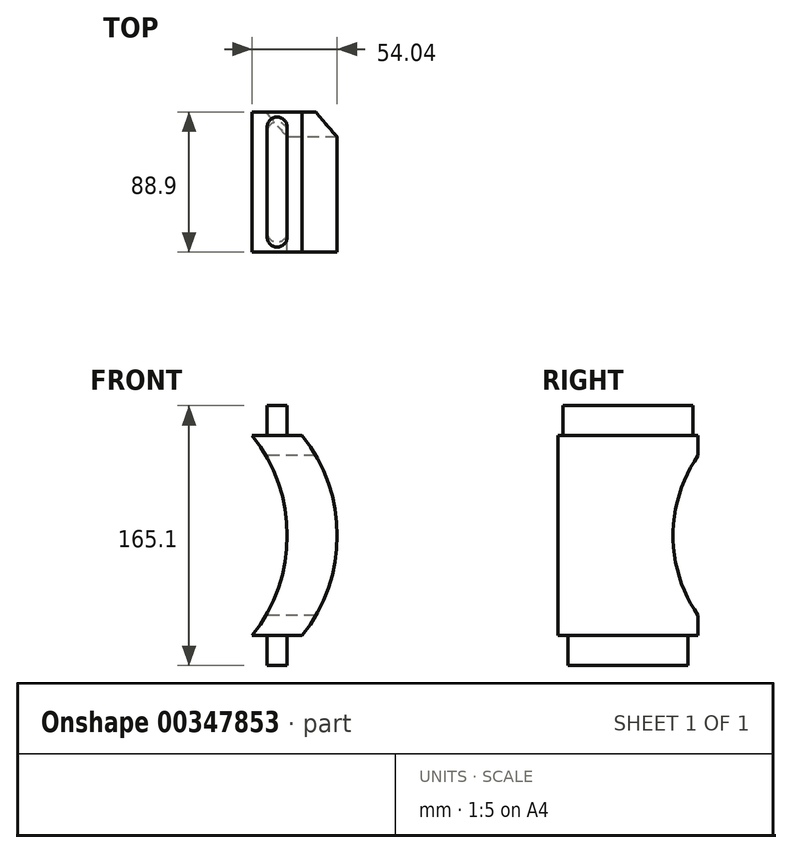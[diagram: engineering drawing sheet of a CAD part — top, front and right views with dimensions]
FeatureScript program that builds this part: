
annotation { "Feature Type Name" : "Feature", "Feature Type Description" : "" }
export const myFeature = defineFeature(function(context is Context, id is Id, definition is map)
    precondition{}
    {
        {
            var Q0;
            Q0=qCreatedBy(makeId("Front.planeOp"),FACE);
            var sketch = newSketch(context, id + "F0", { "sketchPlane" : qUnion([Q0])});
            skLineSegment(sketch, "E0.bottom", {"start": v(-32.55, 106.2) * mm, "end": v(-64.3, 106.2) * mm});
            skLineSegment(sketch, "E0.top", {"start": v(-32.55, -20.8) * mm, "end": v(-64.3, -20.8) * mm});
            skLineSegment(sketch, "E0.left", {"start": v(-32.55, 106.2) * mm, "end": v(-32.55, -20.8) * mm});
            skArc(sketch, "E1", {"start": v(-64.3, -20.8) * mm, "mid": v(-42, 42.7) * mm, "end": v(-64.3, 106.2) * mm});
            skArc(sketch, "E2", {"start": v(-32.55, -20.8) * mm, "mid": v(-10.26, 42.7) * mm, "end": v(-32.55, 106.2) * mm});
            skSolve(sketch);
        }
        {
            var Q0;
            Q0 = qSketchRegion(id + "F0", true);
            extrude(context, id + "F1", {"entities" : qUnion([Q0]), "depth" : 88.9 * mm});
        }
        {
            var Q0;
            Q0=makeQuery(id+"F1.opExtrude","SWEPT_FACE",FACE,{"disambiguationData":[OSD([sQuery(id+"F0.wireOp",EDGE,"E0.top")])]});
            var sketch = newSketch(context, id + "F2", { "sketchPlane" : qUnion([Q0])});
            skLineSegment(sketch, "E3", {"start": v(-48.42, 88.9) * mm, "end": v(-48.42, 0) * mm, "construction": true});
            skLineSegment(sketch, "E4", {"start": v(-32.55, 44.45) * mm, "end": v(-64.3, 44.45) * mm, "construction": true});
            skArc(sketch, "E5", {"start": v(-42.07, 76.2) * mm, "mid": v(-48.42, 82.55) * mm, "end": v(-54.77, 76.2) * mm});
            skArc(sketch, "E6", {"start": v(-54.77, 12.7) * mm, "mid": v(-48.42, 6.35) * mm, "end": v(-42.07, 12.7) * mm});
            skLineSegment(sketch, "E7", {"start": v(-54.77, 76.2) * mm, "end": v(-54.77, 12.7) * mm});
            skLineSegment(sketch, "E8", {"start": v(-42.07, 76.2) * mm, "end": v(-42.07, 12.7) * mm});
            skLineSegment(sketch, "E9", {"start": v(-54.77, 44.45) * mm, "end": v(-42.07, 44.45) * mm, "construction": true});
            skSolve(sketch);
        }
        {
            var Q0;
            Q0 = qSketchRegion(id + "F2", true);
            extrude(context, id + "F3", {"entities" : qUnion([Q0]), "operationType" : NewBodyOperationType.ADD, "depth" : 19.05 * mm});
        }
        {
            var Q0;
            Q0=makeQuery(id+"F1.opExtrude","SWEPT_FACE",FACE,{"disambiguationData":[OSD([sQuery(id+"F0.wireOp",EDGE,"E0.bottom")])]});
            var sketch = newSketch(context, id + "F4", { "sketchPlane" : qUnion([Q0])});
            skLineSegment(sketch, "E10", {"start": v(-48.42, 0) * mm, "end": v(-48.42, -88.9) * mm, "construction": true});
            skLineSegment(sketch, "E11", {"start": v(-32.55, -44.45) * mm, "end": v(-64.3, -44.45) * mm, "construction": true});
            skLineSegment(sketch, "E12", {"start": v(-48.42, -3.17) * mm, "end": v(-48.42, -88.9) * mm, "construction": true});
            skArc(sketch, "E13", {"start": v(-42.07, -9.52) * mm, "mid": v(-48.42, -3.17) * mm, "end": v(-54.77, -9.52) * mm});
            skArc(sketch, "E14", {"start": v(-54.77, -79.38) * mm, "mid": v(-48.42, -85.73) * mm, "end": v(-42.07, -79.38) * mm});
            skLineSegment(sketch, "E15", {"start": v(-54.77, -9.52) * mm, "end": v(-54.77, -79.38) * mm});
            skLineSegment(sketch, "E16", {"start": v(-42.07, -9.52) * mm, "end": v(-42.07, -79.38) * mm});
            skLineSegment(sketch, "E17", {"start": v(-42.07, -44.45) * mm, "end": v(-54.77, -44.45) * mm, "construction": true});
            skSolve(sketch);
        }
        {
            var Q0;
            Q0 = qSketchRegion(id + "F4", true);
            extrude(context, id + "F5", {"entities" : qUnion([Q0]), "operationType" : NewBodyOperationType.ADD, "depth" : 19.05 * mm});
        }
        {
            var Q0;
            Q0=makeQuery(id+"F1.opExtrude","CAP_VERTEX",VERTEX,{"disambiguationData":[OSD([sQuery(id+"F0.wireOp",EDGE,"E0.bottom"),sQuery(id+"F0.wireOp",EDGE,"E1")])],"isStart":true});
            var Q1;
            Q1=makeQuery(id+"F1.opExtrude","CAP_VERTEX",VERTEX,{"disambiguationData":[OSD([sQuery(id+"F0.wireOp",EDGE,"E0.bottom"),sQuery(id+"F0.wireOp",EDGE,"E1")])],"isStart":false});
            var Q2;
            Q2=makeQuery(id+"F1.opExtrude","CAP_VERTEX",VERTEX,{"disambiguationData":[OSD([sQuery(id+"F0.wireOp",EDGE,"E0.top"),sQuery(id+"F0.wireOp",EDGE,"E1")])],"isStart":true});
            cPlane(context, id + "F6", {"entities" : qUnion([Q0, Q1, Q2]), "cplaneType" : CPlaneType.THREE_POINT, "offset" : 25.4 * mm, "width" : 152.4 * mm, "height" : 152.4 * mm});
        }
        {
            var Q0;
            Q0=qCreatedBy(id+"F6.planeOp",FACE);
            var sketch = newSketch(context, id + "F7", { "sketchPlane" : qUnion([Q0])});
            skLineSegment(sketch, "E18", {"start": v(44.45, 126.91) * mm, "end": v(44.45, -53.83) * mm, "construction": true});
            skLineSegment(sketch, "E19", {"start": v(-29.2, 42.7) * mm, "end": v(106.48, 42.7) * mm, "construction": true});
            skArc(sketch, "E20", {"start": v(0, -8.1) * mm, "mid": v(15.88, 42.7) * mm, "end": v(0, 93.5) * mm});
            skLineSegment(sketch, "E21", {"start": v(0, 93.5) * mm, "end": v(-11.49, 93.5) * mm});
            skLineSegment(sketch, "E22", {"start": v(-11.49, 93.5) * mm, "end": v(-11.49, -8.62) * mm});
            skLineSegment(sketch, "E23", {"start": v(-11.49, -8.62) * mm, "end": v(0, -8.1) * mm});
            skArc(sketch, "E24.MirrorCS", {"start": v(88.9, -8.1) * mm, "mid": v(73.03, 42.7) * mm, "end": v(88.9, 93.5) * mm});
            skLineSegment(sketch, "E25.MirrorCS", {"start": v(88.9, 93.5) * mm, "end": v(100.39, 93.5) * mm});
            skLineSegment(sketch, "E26.MirrorCS", {"start": v(100.39, 93.5) * mm, "end": v(100.39, -8.62) * mm});
            skLineSegment(sketch, "E27.MirrorCS", {"start": v(100.39, -8.62) * mm, "end": v(88.9, -8.1) * mm});
            skSolve(sketch);
        }
        {
            var Q0;
            Q0=makeQuery(id+"F7.imprint","IMPRINT",FACE,{"disambiguationData":[TD([[makeQuery(id+"F7.imprint","IMPRINT",EDGE,{"derivedFrom":sQuery(id+"F7.wireOp",EDGE,"E20")}),1.0]])]});
            var Q1;
            Q1=makeQuery(id+"F7.imprint","IMPRINT",FACE,{"disambiguationData":[TD([[makeQuery(id+"F7.imprint","IMPRINT",EDGE,{"derivedFrom":sQuery(id+"F7.wireOp",EDGE,"E24.MirrorCS")}),-1.0]])]});
            extrude(context, id + "F8", {"entities" : qUnion([Q0, Q1]), "operationType" : NewBodyOperationType.REMOVE, "endBound" : BoundingType.THROUGH_ALL, "oppositeDirection" : true, "depth" : 25.4 * mm});
        }
    });
